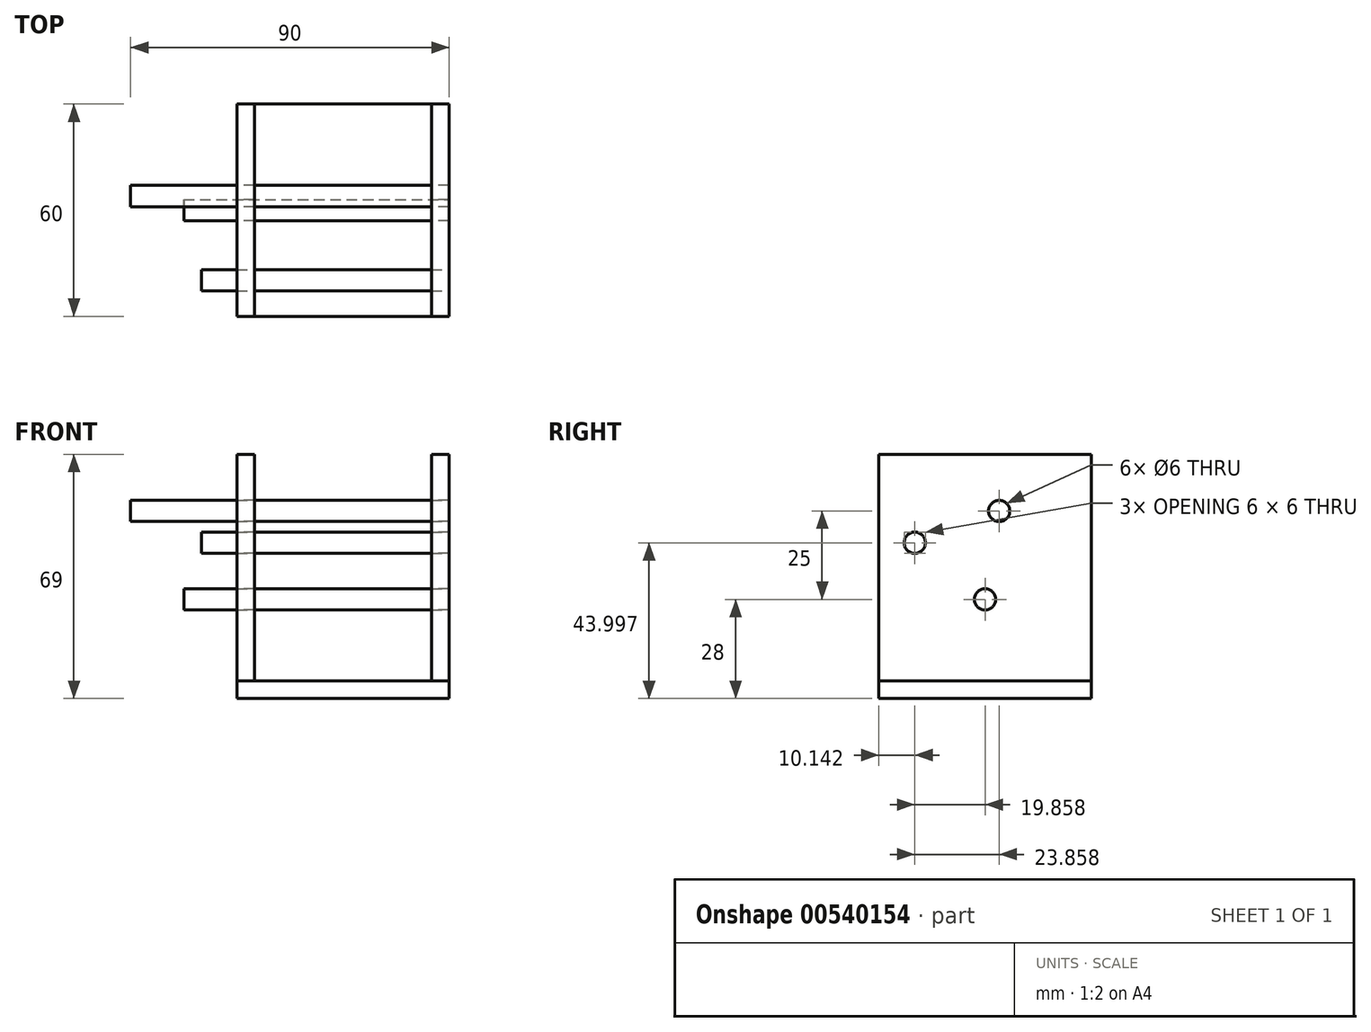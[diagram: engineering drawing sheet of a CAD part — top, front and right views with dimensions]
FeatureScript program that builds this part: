
annotation { "Feature Type Name" : "Feature", "Feature Type Description" : "" }
export const myFeature = defineFeature(function(context is Context, id is Id, definition is map)
    precondition{}
    {
        {
            var Q0;
            Q0=qCreatedBy(makeId("Top.planeOp"),FACE);
            var sketch = newSketch(context, id + "F0", { "sketchPlane" : qUnion([Q0])});
            skLineSegment(sketch, "E0.bottom", {"start": v(0, 0) * mm, "end": v(60, 0) * mm});
            skLineSegment(sketch, "E0.top", {"start": v(0, -60) * mm, "end": v(60, -60) * mm});
            skLineSegment(sketch, "E0.left", {"start": v(0, 0) * mm, "end": v(0, -60) * mm});
            skLineSegment(sketch, "E0.right", {"start": v(60, 0) * mm, "end": v(60, -60) * mm});
            skSolve(sketch);
        }
        {
            var Q0;
            Q0=makeQuery(id+"F0.imprint","IMPRINT",FACE,{"disambiguationData":[TD([[makeQuery(id+"F0.imprint","IMPRINT",EDGE,{"derivedFrom":sQuery(id+"F0.wireOp",EDGE,"E0.bottom")}),-1.0]])]});
            extrude(context, id + "F1", {"entities" : qUnion([Q0]), "depth" : 5 * mm, "offsetDistance" : 25 * mm});
        }
        {
            var Q0;
            Q0=makeQuery(id+"F1.opExtrude","CAP_FACE",FACE,{"disambiguationData":[OSD([sQuery(id+"F0.wireOp",EDGE,"E0.bottom"),sQuery(id+"F0.wireOp",EDGE,"E0.top"),sQuery(id+"F0.wireOp",EDGE,"E0.left"),sQuery(id+"F0.wireOp",EDGE,"E0.right")])],"isStart":false});
            var sketch = newSketch(context, id + "F2", { "sketchPlane" : qUnion([Q0])});
            skLineSegment(sketch, "E1.bottom", {"start": v(60, -60) * mm, "end": v(55, -60) * mm});
            skLineSegment(sketch, "E1.top", {"start": v(60, 0) * mm, "end": v(55, 0) * mm});
            skLineSegment(sketch, "E1.left", {"start": v(60, -60) * mm, "end": v(60, 0) * mm});
            skLineSegment(sketch, "E1.right", {"start": v(55, -60) * mm, "end": v(55, 0) * mm});
            skSolve(sketch);
        }
        {
            var Q0;
            Q0 = qSketchRegion(id + "F2", true);
            extrude(context, id + "F3", {"entities" : qUnion([Q0]), "depth" : 64 * mm, "offsetDistance" : 25 * mm});
        }
        {
            var Q0;
            Q0=makeQuery(id+"F3.opExtrude","SWEPT_BODY",BODY,{"disambiguationData":[OSD([sQuery(id+"F2.wireOp",EDGE,"E1.bottom"),sQuery(id+"F2.wireOp",EDGE,"E1.top"),sQuery(id+"F2.wireOp",EDGE,"E1.left"),sQuery(id+"F2.wireOp",EDGE,"E1.right")])]});
            transform(context, id + "F4", {"entities" : qUnion([Q0]), "transformType" : TransformType.TRANSLATION_3D, "dx" : -40000 * mm, "dy" : 0 * mm, "dz" : 0 * mm, "makeCopy" : true});
        }
        {
            var Q0;
            Q0=makeQuery(id+"F4.opPattern","COPY",BODY,{"derivedFrom":makeQuery(id+"F3.opExtrude","SWEPT_BODY",BODY,{"disambiguationData":[OSD([sQuery(id+"F2.wireOp",EDGE,"E1.bottom"),sQuery(id+"F2.wireOp",EDGE,"E1.top"),sQuery(id+"F2.wireOp",EDGE,"E1.left"),sQuery(id+"F2.wireOp",EDGE,"E1.right")])]}),"instanceName":"1"});
            deleteBodies(context, id + "F5", {"entities" : qUnion([Q0])});
        }
        {
            var Q0;
            Q0=makeQuery(id+"F3.opExtrude","SWEPT_BODY",BODY,{"disambiguationData":[OSD([sQuery(id+"F2.wireOp",EDGE,"E1.bottom"),sQuery(id+"F2.wireOp",EDGE,"E1.top"),sQuery(id+"F2.wireOp",EDGE,"E1.left"),sQuery(id+"F2.wireOp",EDGE,"E1.right")])]});
            var Q1;
            Q1=makeQuery(id+"F1.opExtrude","CAP_EDGE",EDGE,{"disambiguationData":[OSD([sQuery(id+"F0.wireOp",EDGE,"E0.top")])],"isStart":false});
            var Q2;
            Q2=makeQuery(id+"F1.opExtrude","CAP_EDGE",EDGE,{"disambiguationData":[OSD([sQuery(id+"F0.wireOp",EDGE,"E0.top")])],"isStart":false});
            transform(context, id + "F6", {"entities" : qUnion([Q0]), "transformType" : TransformType.TRANSLATION_DISTANCE, "transformDirection" : qUnion([Q2]), "distance" : 55 * mm, "oppositeDirection" : true, "makeCopy" : true});
        }
        {
            var Q0;
            Q0=makeQuery(id+"F6.opPattern","COPY",FACE,{"derivedFrom":makeQuery(id+"F3.opExtrude","SWEPT_FACE",FACE,{"disambiguationData":[OSD([sQuery(id+"F2.wireOp",EDGE,"E1.right")])]}),"instanceName":"1"});
            var sketch = newSketch(context, id + "F7", { "sketchPlane" : qUnion([Q0])});
            skCircle(sketch, "E2", {"center": v(30, 28) * mm, "radius": 3 * mm});
            skCircle(sketch, "E3", {"center": v(49.86, 44) * mm, "radius": 3 * mm});
            skCircle(sketch, "E4", {"center": v(26, 53) * mm, "radius": 3 * mm});
            skLineSegment(sketch, "E5", {"start": v(30, 5) * mm, "end": v(30, 69) * mm, "construction": true});
            skCircle(sketch, "E6", {"center": v(26, 53) * mm, "radius": 5 * mm, "construction": true});
            skCircle(sketch, "E7", {"center": v(49.86, 44) * mm, "radius": 5 * mm, "construction": true});
            skCircle(sketch, "E8", {"center": v(30, 28) * mm, "radius": 21 * mm, "construction": true});
            skCircle(sketch, "E9", {"center": v(30, 28) * mm, "radius": 20.5 * mm, "construction": true});
            skCircle(sketch, "E10", {"center": v(49.86, 44) * mm, "radius": 21 * mm, "construction": true});
            skCircle(sketch, "E11", {"center": v(49.86, 44) * mm, "radius": 20.5 * mm, "construction": true});
            skSolve(sketch);
        }
        {
            var Q0;
            Q0 = qSketchRegion(id + "F7", true);
            var Q1;
            Q1=makeQuery(id+"F3.opExtrude","SWEPT_FACE",FACE,{"disambiguationData":[OSD([sQuery(id+"F2.wireOp",EDGE,"E1.left")])]});
            extrude(context, id + "F8", {"entities" : qUnion([Q0]), "operationType" : NewBodyOperationType.REMOVE, "endBound" : BoundingType.UP_TO_SURFACE, "oppositeDirection" : true, "depth" : 25 * mm, "endBoundEntityFace" : qUnion([Q1]), "offsetDistance" : 25 * mm});
        }
        {
            var Q0;
            Q0=makeQuery(id+"F3.opExtrude","SWEPT_FACE",FACE,{"disambiguationData":[OSD([sQuery(id+"F2.wireOp",EDGE,"E1.left")])]});
            var sketch = newSketch(context, id + "F9", { "sketchPlane" : qUnion([Q0])});
            skCircle(sketch, "E12", {"center": v(-49.86, 44) * mm, "radius": 3 * mm});
            skSolve(sketch);
        }
        {
            var Q0;
            Q0 = qSketchRegion(id + "F9", true);
            var Q1;
            Q1=makeQuery(id+"F6.opPattern","COPY",FACE,{"derivedFrom":makeQuery(id+"F3.opExtrude","SWEPT_FACE",FACE,{"disambiguationData":[OSD([sQuery(id+"F2.wireOp",EDGE,"E1.right")])]}),"instanceName":"1"});
            extrude(context, id + "F10", {"entities" : qUnion([Q0]), "oppositeDirection" : true, "depth" : 70 * mm, "endBoundEntityFace" : qUnion([Q1]), "offsetDistance" : 25 * mm});
        }
        {
            var Q0;
            Q0=makeQuery(id+"F3.opExtrude","SWEPT_FACE",FACE,{"disambiguationData":[OSD([sQuery(id+"F2.wireOp",EDGE,"E1.left")])]});
            var sketch = newSketch(context, id + "F11", { "sketchPlane" : qUnion([Q0])});
            skCircle(sketch, "E13", {"center": v(-26, 53) * mm, "radius": 3 * mm});
            skSolve(sketch);
        }
        {
            var Q0;
            Q0 = qSketchRegion(id + "F11", true);
            var Q1;
            Q1=makeQuery(id+"F6.opPattern","COPY",FACE,{"derivedFrom":makeQuery(id+"F3.opExtrude","SWEPT_FACE",FACE,{"disambiguationData":[OSD([sQuery(id+"F2.wireOp",EDGE,"E1.right")])]}),"instanceName":"1"});
            extrude(context, id + "F12", {"entities" : qUnion([Q0]), "oppositeDirection" : true, "depth" : 90 * mm, "endBoundEntityFace" : qUnion([Q1]), "offsetDistance" : 25 * mm});
        }
        {
            var Q0;
            Q0=makeQuery(id+"F3.opExtrude","SWEPT_FACE",FACE,{"disambiguationData":[OSD([sQuery(id+"F2.wireOp",EDGE,"E1.left")])]});
            var sketch = newSketch(context, id + "F13", { "sketchPlane" : qUnion([Q0])});
            skCircle(sketch, "E14", {"center": v(-30, 28) * mm, "radius": 3 * mm});
            skSolve(sketch);
        }
        {
            var Q0;
            Q0 = qSketchRegion(id + "F13", true);
            var Q1;
            Q1=makeQuery(id+"F6.opPattern","COPY",FACE,{"derivedFrom":makeQuery(id+"F3.opExtrude","SWEPT_FACE",FACE,{"disambiguationData":[OSD([sQuery(id+"F2.wireOp",EDGE,"E1.right")])]}),"instanceName":"1"});
            extrude(context, id + "F14", {"entities" : qUnion([Q0]), "oppositeDirection" : true, "depth" : 75 * mm, "endBoundEntityFace" : qUnion([Q1]), "offsetDistance" : 25 * mm});
        }
    });
